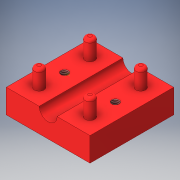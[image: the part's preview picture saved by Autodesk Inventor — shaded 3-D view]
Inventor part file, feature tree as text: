
AUTODESK INVENTOR PART (.ipt)
format: ipt  version: 2016 SP1 (Build 200210100, 210)  size: 164,352 bytes
history: native  units: in
note: dims shown in document units (in); Inventor stores cm internally (conversion verified against a paired STEP export)
features: sketch x5, extrude x3, hole x1, fillet x1
ambient origin geometry x8: Origin, YZ Plane, XZ Plane, XY Plane, X Axis, Y Axis, Z Axis, Center Point
bodies: Solid1 (feature_tree)
feature tree (10):
  extrude  "Extrusion1"  Depth=0.5in
  extrude  "Extrusion2"  Depth=0.375in
  hole  "Hole1"  [1 undecoded]
  extrude  "Extrusion3"  Depth=0.3438in
  fillet  "Fillet1"  Radius=0.875in
  sketch  "Sketch1"  dims[d0=1.75in d1=0.5in]
  sketch  "Sketch2"  dims[d2=0.0in d3=0.375in]
  sketch  "Sketch3"  dims[d4=1.0in d5=0.0in]
  sketch  "Sketch4"  dims[d6=0.3438in d7=0.3438in]
  sketch  "Sketch7"  dims[d8=0.156in d9=0.38in d10=0.385in d11=0.25in d12=0.5635in d13=0.536in d14=0.8108in d22=0.875in d23=0.875in d26=0.3438in d27=0.3438in d28=0.2in d29=0.4in d30=0.0in d31=0.0625in]
note: 1 required parameter value undecoded (feature->parameter linkage not recoverable at this tier; creation-order binding heuristic only, values carry confidence <= 0.55)
